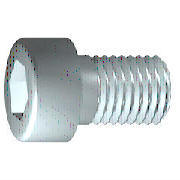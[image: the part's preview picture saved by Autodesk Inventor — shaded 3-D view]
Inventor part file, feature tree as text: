
AUTODESK INVENTOR PART (.ipt)
format: ipt  version: 2020 (Build 240168000, 168)  size: 187,392 bytes
history: native  units: mm (DEFAULTED — no unit token found)
features: sketch x2, other x1, extrude x1, plane x1, fillet x1
ambient origin geometry x7: Origin, YZ Plane, XY Plane, X Axis, Y Axis, Z Axis, Center Point
bodies: Solid1 (feature_tree)
feature tree (6):
  other  "Bryła"
  extrude  "Szczelina"  Depth=22.0mm
  plane  "Work Plane1"
  fillet  "Fillet2"  Radius=0.49086mm
  sketch  "Szkic1"
  sketch  "Szkic2"
